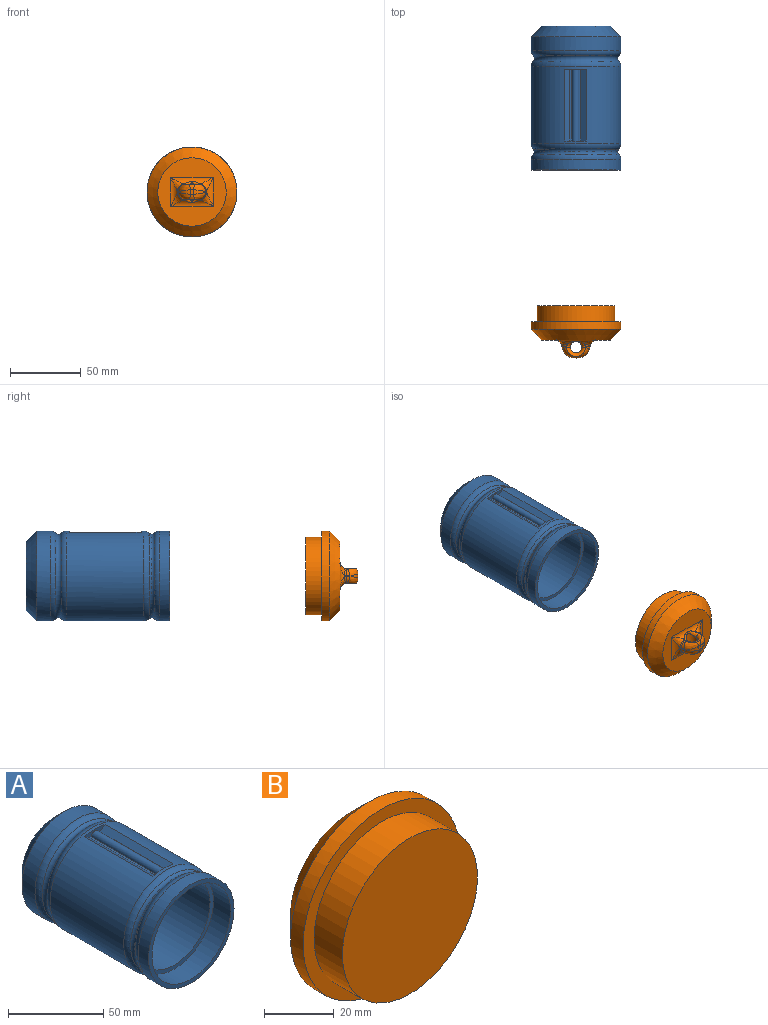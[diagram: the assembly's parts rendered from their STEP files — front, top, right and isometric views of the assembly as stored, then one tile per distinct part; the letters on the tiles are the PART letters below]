
ASSEMBLY  parts=2 mates=1
PART A: 26 faces, bbox 69.3x101.6x69.3 mm
  f0: plane 50.8x1.27mm, normal (-0.02,0,1), area 64.6mm2, adj f1,f20,f22,f24
  f1: plane 15.24x3.62mm, normal (0,1,0), area 29.4mm2, adj f0,f2,f5,f22,f23,f24
  f2: plane 50.8x1.27mm, normal (-0.02,0,1), area 64.6mm2, adj f1,f20,f23,f24
  f3: plane 15.24x1.28mm, normal (0,1,0), area 0.3mm2, adj f6,f21
  f4: plane 15.24x1.28mm, normal (0,-1,0), area 0.3mm2, adj f6,f21
  f5: cylinder r=31.75mm len=63.5mm, axis (0,1,0), area 10128.4mm2, adj f1,f13,f18,f20,f22,f23
  f6: cylinder r=26.67mm len=83.82mm, axis (0,1,0), area 13260.7mm2, adj f3,f4,f10,f11,f21
  f7: cylinder r=31.75mm len=63.5mm, axis (0,1,0), area 1500.7mm2, adj f8,f14
  f8: plane 63.5x63.5mm, normal (0,-1,0), area 486.4mm2, adj f7,f9
  f9: cylinder r=29.21mm len=58.42mm, axis (0,-1,0), area 2330.9mm2, adj f8,f10
  f10: plane 58.42x58.42mm, normal (0,-1,0), area 445.9mm2, adj f6,f9
  f11: plane 53.34x53.34mm, normal (0,-1,0), area 2234.6mm2, adj f6
  f12: torus R=32mm, axis (0,1,0), area 755.8mm2, adj f13,f14
  f13: torus R=26.67mm, axis (0,1,0), area 794.2mm2, adj f5,f12
  f14: torus R=26.67mm, axis (0,-1,0), area 794.2mm2, adj f7,f12
  f15: torus R=31.82mm, axis (0,-1,0), area 782.2mm2, adj f18,f19
  f16: plane 48.26x48.26mm, normal (0,1,0), area 1829.2mm2, adj f25
  f17: cylinder r=31.75mm len=63.5mm, axis (0,1,0), area 1921.3mm2, adj f19,f25
  f18: torus R=26.67mm, axis (0,-1,0), area 825.4mm2, adj f5,f15
  f19: torus R=26.67mm, axis (0,1,0), area 825.4mm2, adj f15,f17
  f20: plane 15.24x3.62mm, normal (0,-1,0), area 29.4mm2, adj f0,f2,f5,f22,f23,f24
  f21: cylinder r=26.07mm len=50.8mm, axis (0,1,0), area 785.8mm2, adj f3,f4,f6
  f22: plane 50.8x3.81mm, normal (0.56,0,0.83), area 233.8mm2, adj f0,f1,f5,f20
  f23: plane 50.8x3.81mm, normal (-0.58,0,0.82), area 236.7mm2, adj f1,f2,f5,f20
  f24: cylinder r=2.54mm len=50.8mm, axis (0,-1,0), area 405.4mm2, adj f0,f1,f2,f20
  f25: cone r=31.75mm half-angle=45deg, axis (0,-1,0), area 1891.8mm2, adj f16,f17
PART B: 36 faces, bbox 63.5x38.4x63.5 mm
  f0: cylinder r=31.75mm len=63.5mm, axis (0,1,0), area 1013.4mm2, adj f1,f5
  f1: plane 63.5x63.5mm, normal (0,-1,0), area 824.6mm2, adj f0,f3
  f2: plane 48.26x48.26mm, normal (0,1,0), area 1224.7mm2, adj f5,f10,f11,f12,f13
  f3: cylinder r=27.31mm len=54.61mm, axis (0,1,0), area 1961mm2, adj f1,f4
  f4: plane 54.61x54.61mm, normal (0,-1,0), area 2342.3mm2, adj f3
  f5: cone r=31.75mm half-angle=45deg, axis (0,-1,0), area 1891.8mm2, adj f0,f2
  f6: plane 4.08x1.61mm, normal (0,1,0), area 6.4mm2, adj f7,f8,f22,f31
  f7: cylinder r=9.2mm len=9.14mm, axis (0,0,-1), area 25.8mm2, adj f6,f11,f23,f24,f29,f30
  f8: cylinder r=9.2mm len=9.14mm, axis (0,0,1), area 25.8mm2, adj f6,f12,f20,f21,f32,f33
  f9: cylinder r=4.13mm len=12.78mm, axis (0,0,-1), area 174.1mm2, adj f14,f15,f16,f17
  f10: cylinder r=5.08mm len=29.99mm, axis (1,0,0), area 94.6mm2, adj f2,f15,f18,f26
  f11: cylinder r=5.08mm len=20.16mm, axis (0,0,-1), area 58.5mm2, adj f2,f7,f25,f26,f27,f28
  f12: cylinder r=5.08mm len=20.16mm, axis (0,0,1), area 58.5mm2, adj f2,f8,f18,f19,f34,f35
  f13: cylinder r=5.08mm len=29.99mm, axis (-1,0,0), area 94.6mm2, adj f2,f17,f27,f35
  f14: torus R=6.67mm, axis (0,0,-1), area 63.3mm2, adj f9,f15,f21,f22,f23
  f15: bspline ~13.34x5.27mm, area 41.7mm2, adj f9,f10,f14,f19,f20,f24,f25
  f16: torus R=6.67mm, axis (0,0,-1), area 63.3mm2, adj f9,f17,f30,f31,f32
  f17: bspline ~13.34x5.27mm, area 41.7mm2, adj f9,f13,f16,f28,f29,f33,f34
  f18: bspline ~9.53x9.53mm, area 21.5mm2, adj f10,f12,f19
  f19: bspline ~5.22x4.59mm, area 7.6mm2, adj f12,f15,f18,f20
  f20: bspline ~4.8x3.39mm, area 10.7mm2, adj f8,f15,f19,f21
  f21: bspline ~8.5x7.62mm, area 46.5mm2, adj f8,f14,f20,f22
  f22: bspline ~4.01x3.13mm, area 9.4mm2, adj f6,f14,f21,f23
  f23: bspline ~8.5x7.62mm, area 46.5mm2, adj f7,f14,f22,f24
  f24: bspline ~4.8x3.39mm, area 10.7mm2, adj f7,f15,f23,f25
  f25: bspline ~5.22x4.59mm, area 7.6mm2, adj f11,f15,f24,f26
  f26: bspline ~9.2x9.18mm, area 34.2mm2, adj f10,f11,f25
  f27: bspline ~9.2x9.18mm, area 34.2mm2, adj f11,f13,f28
  f28: bspline ~5.22x4.59mm, area 7.6mm2, adj f11,f17,f27,f29
  f29: bspline ~4.8x3.39mm, area 10.7mm2, adj f7,f17,f28,f30
  f30: bspline ~8.5x7.62mm, area 46.5mm2, adj f7,f16,f29,f31
  f31: bspline ~4.01x3.13mm, area 9.4mm2, adj f6,f16,f30,f32
  f32: bspline ~8.5x7.62mm, area 46.5mm2, adj f8,f16,f31,f33
  f33: bspline ~4.8x3.39mm, area 10.7mm2, adj f8,f17,f32,f34
  f34: bspline ~5.22x4.59mm, area 7.6mm2, adj f12,f17,f33,f35
  f35: bspline ~9.53x9.53mm, area 21.5mm2, adj f12,f13,f34
PLACE A t=(-12.37,60.53,-28.8)mm
PLACE B rot(axis=(0,0,1),180deg) t=(-122.95,-161.05,-28.8)mm
MATE slider B.f0 <-> A.f5  axis (0,1,0) through (-12.37,-148.35,-28.8)mm
